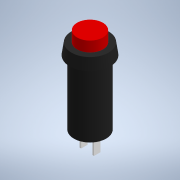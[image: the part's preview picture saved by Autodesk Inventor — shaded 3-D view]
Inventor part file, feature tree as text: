
AUTODESK INVENTOR PART (.ipt)
format: ipt  version: 2021 (Build 250183000, 183)  size: 139,776 bytes
history: native  units: mm
features: sketch x2, revolve x1, extrude x1
ambient origin geometry x8: Origin, YZ Plane, XZ Plane, XY Plane, X Axis, Y Axis, Z Axis, Center Point
bodies: Solid1 (feature_tree)
feature tree (4):
  revolve  "Revolution1"  [1 undecoded]
  extrude  "Extrusion1"  Depth=3.5mm
  sketch  "Sketch1"  dims[d0=4.0mm d1=5.75mm]
  sketch  "Sketch2"  dims[d2=6.25mm d3=3.5mm d4=3.2mm d5=20.0mm d6=5.0mm d7=90.0deg d8=3.5mm d9=1.75mm d10=2.0mm d11=0.5mm d12=5.5mm d13=0.0mm]
note: 1 required parameter value undecoded (feature->parameter linkage not recoverable at this tier; creation-order binding heuristic only, values carry confidence <= 0.55)
